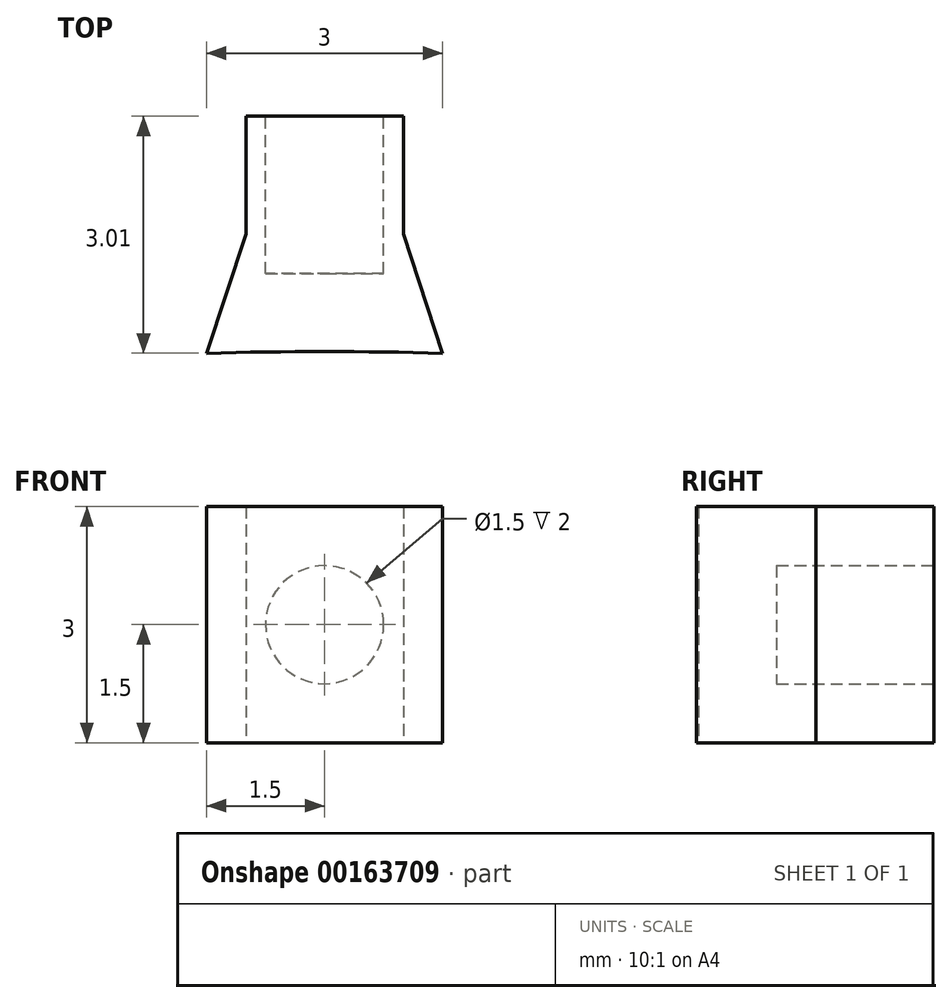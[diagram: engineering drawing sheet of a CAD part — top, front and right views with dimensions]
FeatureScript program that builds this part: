
annotation { "Feature Type Name" : "Feature", "Feature Type Description" : "" }
export const myFeature = defineFeature(function(context is Context, id is Id, definition is map)
    precondition{}
    {
        {
            var Q0;
            Q0=qCreatedBy(makeId("Top.planeOp"),FACE);
            var sketch = newSketch(context, id + "F0", { "sketchPlane" : qUnion([Q0])});
            skLineSegment(sketch, "E0", {"start": v(-1.5, -1.52) * mm, "end": v(-1, -0.01) * mm});
            skLineSegment(sketch, "E1", {"start": v(-1, -0.01) * mm, "end": v(-1, 1.49) * mm});
            skArc(sketch, "E2", {"start": v(1.5, -1.52) * mm, "mid": v(0, -1.5) * mm, "end": v(-1.5, -1.52) * mm});
            skLineSegment(sketch, "E3", {"start": v(0, 1.5) * mm, "end": v(0, -1.5) * mm, "construction": true});
            skLineSegment(sketch, "E4.MirrorCS", {"start": v(1, -0.01) * mm, "end": v(1, 1.49) * mm});
            skLineSegment(sketch, "E5.MirrorCS", {"start": v(1.5, -1.52) * mm, "end": v(1, -0.01) * mm});
            skLineSegment(sketch, "E6", {"start": v(-1, 1.49) * mm, "end": v(1, 1.49) * mm});
            skSolve(sketch);
        }
        {
            var Q0;
            Q0 = qSketchRegion(id + "F0", true);
            extrude(context, id + "F1", {"entities" : qUnion([Q0]), "depth" : 3 * mm});
        }
        {
            var Q0;
            Q0=makeQuery(id+"F1.opExtrude","SWEPT_FACE",FACE,{"disambiguationData":[OSD([sQuery(id+"F0.wireOp",EDGE,"E6")])]});
            var sketch = newSketch(context, id + "F2", { "sketchPlane" : qUnion([Q0])});
            skCircle(sketch, "E7", {"center": v(0, 1.5) * mm, "radius": 0.75 * mm});
            skSolve(sketch);
        }
        {
            var Q0;
            Q0 = qSketchRegion(id + "F2", true);
            extrude(context, id + "F3", {"entities" : qUnion([Q0]), "operationType" : NewBodyOperationType.REMOVE, "oppositeDirection" : true, "depth" : 2 * mm});
        }
    });
